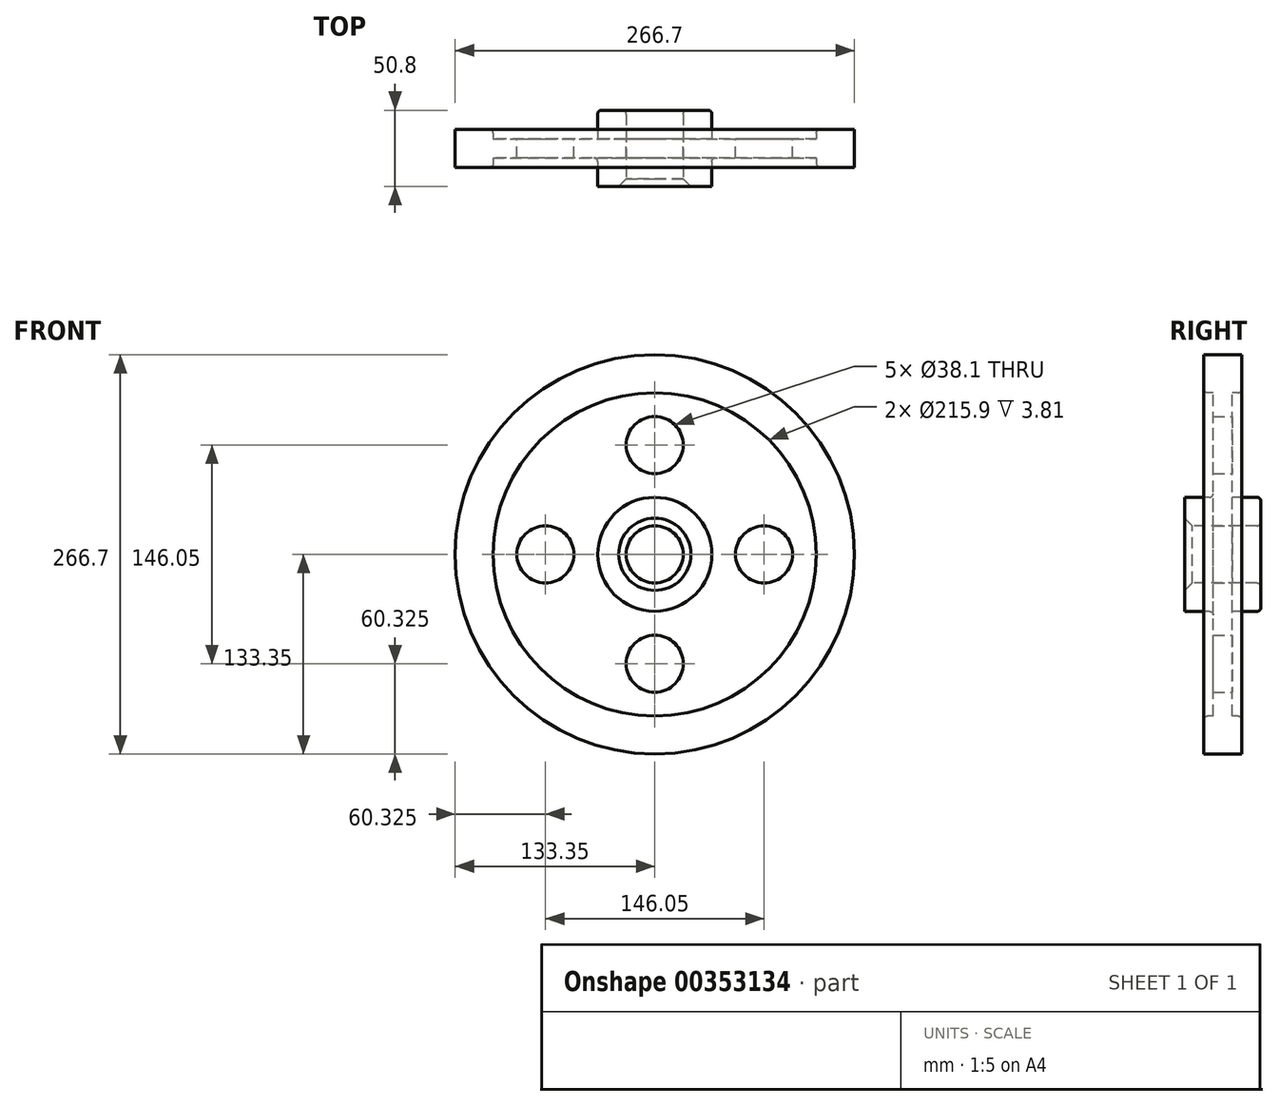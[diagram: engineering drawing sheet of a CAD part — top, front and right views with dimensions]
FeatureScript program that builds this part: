
annotation { "Feature Type Name" : "Feature", "Feature Type Description" : "" }
export const myFeature = defineFeature(function(context is Context, id is Id, definition is map)
    precondition{}
    {
        {
            var Q0;
            Q0=qCreatedBy(makeId("Right.planeOp"),FACE);
            var sketch = newSketch(context, id + "F0", { "sketchPlane" : qUnion([Q0])});
            skLineSegment(sketch, "E0", {"start": v(0, 0) * mm, "end": v(76.2, 0) * mm, "construction": true});
            skLineSegment(sketch, "E1.0", {"start": v(0, 19.05) * mm, "end": v(25.4, 19.05) * mm});
            skLineSegment(sketch, "E2.0", {"start": v(6.35, 38.1) * mm, "end": v(25.4, 38.1) * mm});
            skLineSegment(sketch, "E3.0", {"start": v(6.35, 107.95) * mm, "end": v(12.7, 107.95) * mm});
            skLineSegment(sketch, "E4.0", {"start": v(0, 133.35) * mm, "end": v(6.35, 133.35) * mm});
            skLineSegment(sketch, "E5", {"start": v(0, 0) * mm, "end": v(0, 133.35) * mm, "construction": true});
            skLineSegment(sketch, "E6.0", {"start": v(25.4, 19.05) * mm, "end": v(25.4, 38.1) * mm, "construction": true});
            skLineSegment(sketch, "E7.0", {"start": v(25.4, 19.05) * mm, "end": v(25.4, 38.1) * mm});
            skLineSegment(sketch, "E8.trimOffspring", {"start": v(12.7, 107.95) * mm, "end": v(12.7, 133.35) * mm});
            skLineSegment(sketch, "E9.trimOffspring", {"start": v(6.35, 38.1) * mm, "end": v(6.35, 107.95) * mm});
            skLineSegment(sketch, "E10", {"start": v(0, 133.35) * mm, "end": v(12.7, 133.35) * mm});
            skLineSegment(sketch, "E11.MirrorCS", {"start": v(-12.7, 107.95) * mm, "end": v(-12.7, 133.35) * mm});
            skLineSegment(sketch, "E12.MirrorCS", {"start": v(0, 133.35) * mm, "end": v(-12.7, 133.35) * mm});
            skLineSegment(sketch, "E13.MirrorCS", {"start": v(-6.35, 107.95) * mm, "end": v(-12.7, 107.95) * mm});
            skLineSegment(sketch, "E14.MirrorCS", {"start": v(-6.35, 38.1) * mm, "end": v(-6.35, 107.95) * mm});
            skLineSegment(sketch, "E15.MirrorCS", {"start": v(-6.35, 38.1) * mm, "end": v(-25.4, 38.1) * mm});
            skLineSegment(sketch, "E16.MirrorCS", {"start": v(-25.4, 19.05) * mm, "end": v(-25.4, 38.1) * mm});
            skLineSegment(sketch, "E17.MirrorCS", {"start": v(0, 19.05) * mm, "end": v(-25.4, 19.05) * mm});
            skSolve(sketch);
        }
        {
            var Q0;
            Q0=makeQuery(id+"F0.imprint","IMPRINT",FACE,{"disambiguationData":[TD([[makeQuery(id+"F0.imprint","IMPRINT",EDGE,{"derivedFrom":sQuery(id+"F0.wireOp",EDGE,"E1.0")}),1.0]])]});
            var Q1;
            Q1=sQuery(id+"F0.wireOp",EDGE,"E0");
            revolve(context, id + "F1", {"entities" : qUnion([Q0]), "axis" : qUnion([Q1]), "revolveType" : RevolveType.FULL});
        }
        {
            var Q0;
            Q0=makeQuery(id+"F1.opRevolve","SWEPT_FACE",FACE,{"disambiguationData":[OSD([sQuery(id+"F0.wireOp",EDGE,"E9.trimOffspring")])]});
            var sketch = newSketch(context, id + "F2", { "sketchPlane" : qUnion([Q0])});
            skLineSegment(sketch, "E18", {"start": v(0, 0) * mm, "end": v(0, 73.03) * mm});
            skCircle(sketch, "E19", {"center": v(0, 73.03) * mm, "radius": 19.05 * mm});
            skCircle(sketch, "E20.1.0", {"center": v(-73.03, 0) * mm, "radius": 19.05 * mm});
            skCircle(sketch, "E20.2.0", {"center": v(0, -73.03) * mm, "radius": 19.05 * mm});
            skCircle(sketch, "E20.3.0", {"center": v(73.03, 0) * mm, "radius": 19.05 * mm});
            skPoint(sketch, "E20.center", {"position": v(0, 0) * mm});
            skSolve(sketch);
        }
        {
            var Q0;
            Q0=makeQuery(id+"F2.imprint","IMPRINT",FACE,{"disambiguationData":[TD([[makeQuery(id+"F2.imprint","IMPRINT",EDGE,{"derivedFrom":sQuery(id+"F2.wireOp",EDGE,"E19")}),1.0]])]});
            var Q1;
            Q1=makeQuery(id+"F2.imprint","IMPRINT",FACE,{"disambiguationData":[TD([[makeQuery(id+"F2.imprint","IMPRINT",EDGE,{"derivedFrom":sQuery(id+"F2.wireOp",EDGE,"E20.3.0")}),1.0]])]});
            var Q2;
            Q2=makeQuery(id+"F2.imprint","IMPRINT",FACE,{"disambiguationData":[TD([[makeQuery(id+"F2.imprint","IMPRINT",EDGE,{"derivedFrom":sQuery(id+"F2.wireOp",EDGE,"E20.2.0")}),1.0]])]});
            var Q3;
            Q3=makeQuery(id+"F2.imprint","IMPRINT",FACE,{"disambiguationData":[TD([[makeQuery(id+"F2.imprint","IMPRINT",EDGE,{"derivedFrom":sQuery(id+"F2.wireOp",EDGE,"E20.1.0")}),1.0]])]});
            extrude(context, id + "F3", {"entities" : qUnion([Q0, Q1, Q2, Q3]), "operationType" : NewBodyOperationType.REMOVE, "oppositeDirection" : true, "depth" : 25.4 * mm});
        }
        {
            var Q0;
            Q0=makeQuery(id+"F1.opRevolve","SWEPT_FACE",FACE,{"disambiguationData":[OSD([sQuery(id+"F0.wireOp",EDGE,"E7.0")])]});
            var Q1;
            Q1=makeQuery(id+"F1.opRevolve","SWEPT_EDGE",EDGE,{"disambiguationData":[OSD([sQuery(id+"F0.wireOp",EDGE,"E3.0"),sQuery(id+"F0.wireOp",EDGE,"E8.trimOffspring")])]});
            var Q2;
            Q2=makeQuery(id+"F1.opRevolve","SWEPT_EDGE",EDGE,{"disambiguationData":[OSD([sQuery(id+"F0.wireOp",EDGE,"E14.MirrorCS"),sQuery(id+"F0.wireOp",EDGE,"E15.MirrorCS")])]});
            var Q3;
            Q3=makeQuery(id+"F1.opRevolve","SWEPT_EDGE",EDGE,{"disambiguationData":[OSD([sQuery(id+"F0.wireOp",EDGE,"E11.MirrorCS"),sQuery(id+"F0.wireOp",EDGE,"E13.MirrorCS")])]});
            fillet(context, id + "F4", {"entities" : qUnion([Q0, Q1, Q2, Q3]), "radius" : 2.54 * mm, "tangentPropagation" : true, "allowEdgeOverflow" : false});
        }
        {
            var Q0;
            Q0=makeQuery(id+"F1.opRevolve","SWEPT_FACE",FACE,{"disambiguationData":[OSD([sQuery(id+"F0.wireOp",EDGE,"E1.0"),sQuery(id+"F0.wireOp",EDGE,"E17.MirrorCS")])]});
            var Q1;
            {var subQ0=sQuery(id+"F0.wireOp",EDGE,"E7.0");Q1=makeQuery(id+"F4.opFillet","BLEND_EDGE",EDGE,{"blendedFrom":[makeQuery(id+"F1.opRevolve","SWEPT_EDGE",EDGE,{"disambiguationData":[OSD([sQuery(id+"F0.wireOp",EDGE,"E1.0"),subQ0])]}),makeQuery(id+"F1.opRevolve","SWEPT_FACE",FACE,{"disambiguationData":[OSD([subQ0])]})],"blendedInto":[makeQuery(id+"F1.opRevolve","SWEPT_FACE",FACE,{"disambiguationData":[OSD([subQ0])]})]});}
            var Q2;
            Q2=makeQuery(id+"F1.opRevolve","SWEPT_EDGE",EDGE,{"disambiguationData":[OSD([sQuery(id+"F0.wireOp",EDGE,"E16.MirrorCS"),sQuery(id+"F0.wireOp",EDGE,"E17.MirrorCS")])]});
            chamfer(context, id + "F5", {"entities" : qUnion([Q0, Q1, Q2]), "width" : 5.08 * mm, "tangentPropagation" : true});
        }
    });
